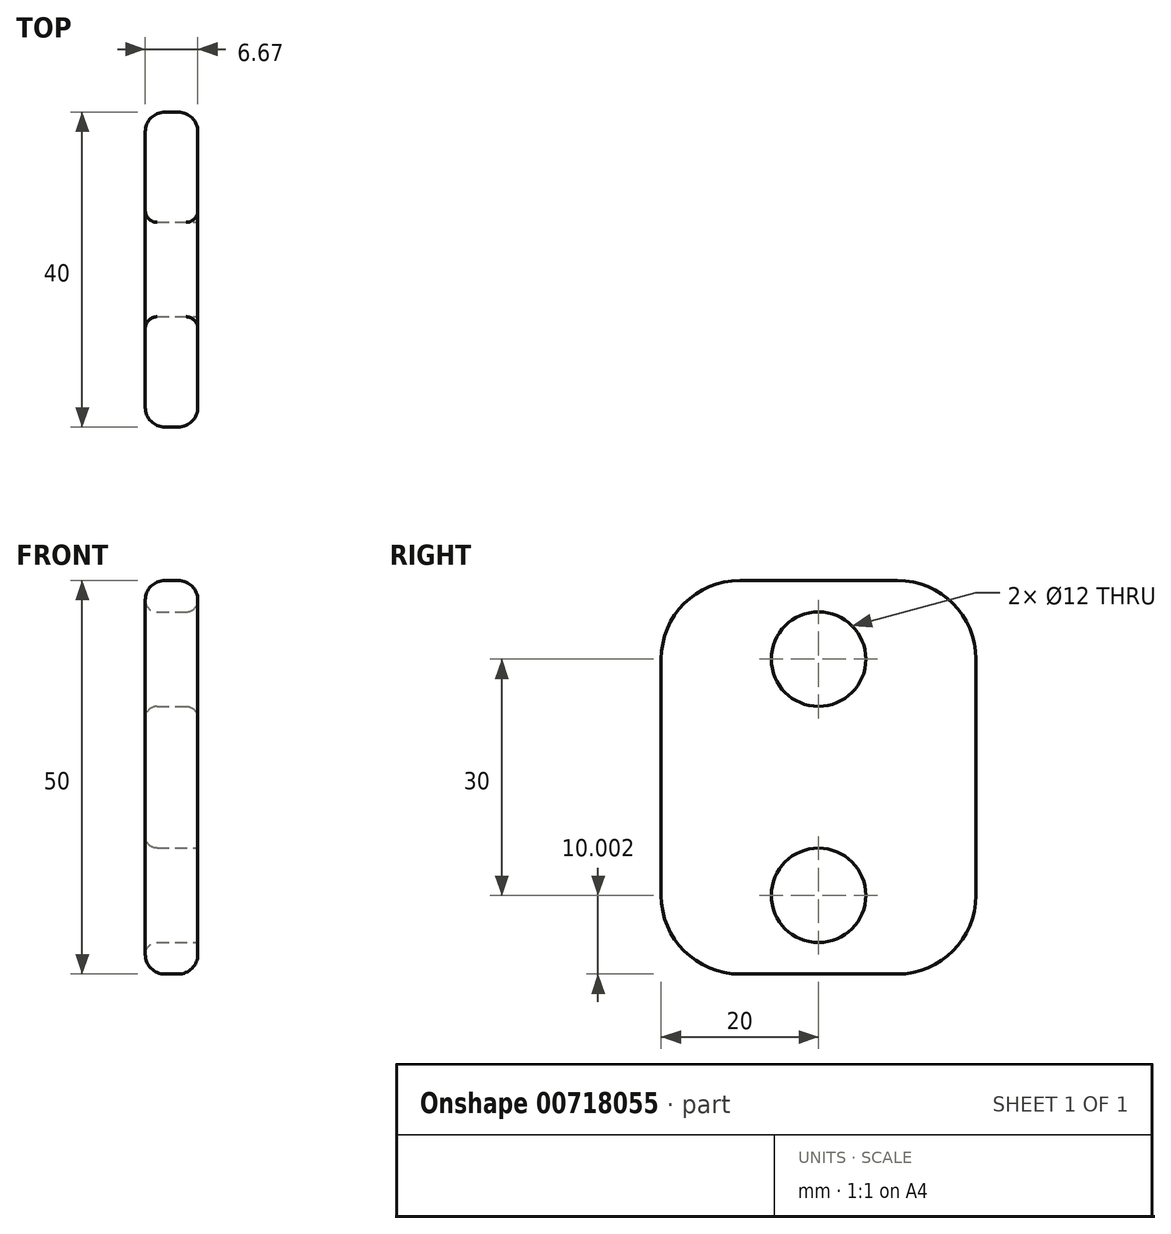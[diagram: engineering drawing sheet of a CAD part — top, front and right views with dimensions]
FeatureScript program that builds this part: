
annotation { "Feature Type Name" : "Feature", "Feature Type Description" : "" }
export const myFeature = defineFeature(function(context is Context, id is Id, definition is map)
    precondition{}
    {
        {
            var Q0;
            Q0=qCreatedBy(makeId("Front.planeOp"),FACE);
            var sketch = newSketch(context, id + "F0", { "sketchPlane" : qUnion([Q0])});
            skLineSegment(sketch, "E0", {"start": v(-3.34, -0.89) * mm, "end": v(-3.34, 19.11) * mm});
            skLineSegment(sketch, "E1", {"start": v(-3.34, 19.11) * mm, "end": v(3.33, 19.11) * mm});
            skLineSegment(sketch, "E2", {"start": v(3.33, 19.11) * mm, "end": v(3.33, -0.89) * mm});
            skLineSegment(sketch, "E3", {"start": v(-3.34, -0.89) * mm, "end": v(-3.34, -30.89) * mm});
            skLineSegment(sketch, "E4", {"start": v(-3.34, -30.89) * mm, "end": v(3.33, -30.89) * mm});
            skLineSegment(sketch, "E5", {"start": v(3.33, -30.89) * mm, "end": v(3.33, 13.67) * mm});
            skLineSegment(sketch, "E6", {"start": v(3.33, -0.89) * mm, "end": v(3.33, 13.67) * mm});
            skSolve(sketch);
        }
        {
            var Q0;
            {var subQ10=sQuery(id+"F0.wireOp",EDGE,"JQoUM4ua-fbHj-mR0V-2uyi-QJGCKq251QAs");Q0=makeQuery(id+"F0.imprint","IMPRINT",FACE,{"disambiguationData":[TD([[makeQuery(id+"F0.imprint","IMPRINT",EDGE,{"derivedFrom":subQ10}),-1.0]])]});}
            var Q1;
            {var subQ0=sQuery(id+"F0.wireOp",EDGE,"E0");Q1=makeQuery(id+"F0.imprint","IMPRINT",FACE,{"disambiguationData":[TD([[makeQuery(id+"F0.imprint","IMPRINT",EDGE,{"derivedFrom":subQ0}),-1.0]])]});}
            var Q2;
            Q2=makeQuery(id+"F0.imprint","IMPRINT",FACE,{"disambiguationData":[TD([[makeQuery(id+"F0.imprint","IMPRINT",EDGE,{"derivedFrom":sQuery(id+"F0.wireOp",EDGE,"YiIlp7im-Q15v-nGEx-m55B-phNHHMeuZ1Th")}),-1.0]])]});
            var Q3;
            {var subQ1=sQuery(id+"F0.wireOp",EDGE,"EbttIiGy-8kt3-poWc-bNZX-1UF2vUk4pGtZ");Q3=makeQuery(id+"F0.imprint","IMPRINT",FACE,{"disambiguationData":[TD([[makeQuery(id+"F0.imprint","IMPRINT",EDGE,{"derivedFrom":subQ1}),1.0]])]});}
            extrude(context, id + "F1", {"entities" : qUnion([Q0, Q1, Q2, Q3]), "depth" : 40 * mm, "offsetDistance" : 25 * mm});
        }
        {
            var Q0;
            Q0=makeQuery(id+"F1.opExtrude","SWEPT_FACE",FACE,{"disambiguationData":[OSD([sQuery(id+"F0.wireOp",EDGE,"E2"),sQuery(id+"F0.wireOp",EDGE,"E5"),sQuery(id+"F0.wireOp",EDGE,"E6")])]});
            var sketch = newSketch(context, id + "F2", { "sketchPlane" : qUnion([Q0])});
            skLineSegment(sketch, "E7", {"start": v(-20, 19.11) * mm, "end": v(-20, -30.89) * mm, "construction": true});
            skLineSegment(sketch, "E8", {"start": v(-20, 19.11) * mm, "end": v(-20, 9.11) * mm, "construction": true});
            skLineSegment(sketch, "E9", {"start": v(-20, 9.11) * mm, "end": v(-20, 0) * mm, "construction": true});
            skLineSegment(sketch, "E10", {"start": v(-20, 0) * mm, "end": v(-20, -10) * mm, "construction": true});
            skLineSegment(sketch, "E11", {"start": v(-20, -10) * mm, "end": v(-20, -20.89) * mm, "construction": true});
            skLineSegment(sketch, "E12", {"start": v(-20, -20.89) * mm, "end": v(-20, -30.89) * mm, "construction": true});
            skCircle(sketch, "E13", {"center": v(-20, 9.11) * mm, "radius": 6 * mm});
            skCircle(sketch, "E14", {"center": v(-20, -20.89) * mm, "radius": 6 * mm});
            skSolve(sketch);
        }
        {
            var Q0;
            Q0=makeQuery(id+"F2.imprint","IMPRINT",FACE,{"disambiguationData":[TD([[makeQuery(id+"F2.imprint","IMPRINT",EDGE,{"derivedFrom":sQuery(id+"F2.wireOp",EDGE,"E13")}),1.0]])]});
            var Q1;
            Q1=makeQuery(id+"F2.imprint","IMPRINT",FACE,{"disambiguationData":[TD([[makeQuery(id+"F2.imprint","IMPRINT",EDGE,{"derivedFrom":sQuery(id+"F2.wireOp",EDGE,"E14")}),1.0]])]});
            extrude(context, id + "F3", {"entities" : qUnion([Q0, Q1]), "operationType" : NewBodyOperationType.REMOVE, "oppositeDirection" : true, "depth" : 25 * mm, "offsetDistance" : 25 * mm});
        }
        {
            var Q0;
            Q0=makeQuery(id+"F1.opExtrude","CAP_EDGE",EDGE,{"disambiguationData":[OSD([sQuery(id+"F0.wireOp",EDGE,"E1")])],"isStart":false});
            var Q1;
            Q1=makeQuery(id+"F1.opExtrude","CAP_EDGE",EDGE,{"disambiguationData":[OSD([sQuery(id+"F0.wireOp",EDGE,"E1")])],"isStart":true});
            var Q2;
            Q2=makeQuery(id+"F1.opExtrude","CAP_EDGE",EDGE,{"disambiguationData":[OSD([sQuery(id+"F0.wireOp",EDGE,"E4")])],"isStart":true});
            var Q3;
            Q3=makeQuery(id+"F1.opExtrude","CAP_EDGE",EDGE,{"disambiguationData":[OSD([sQuery(id+"F0.wireOp",EDGE,"E4")])],"isStart":false});
            fillet(context, id + "F4", {"entities" : qUnion([Q0, Q1, Q2, Q3]), "radius" : 10 * mm, "tangentPropagation" : true, "allowEdgeOverflow" : false});
        }
        {
            var Q0;
            Q0=makeQuery(id+"F1.opExtrude","SWEPT_EDGE",EDGE,{"disambiguationData":[OSD([sQuery(id+"F0.wireOp",EDGE,"E1"),sQuery(id+"F0.wireOp",EDGE,"E2")])]});
            var Q1;
            Q1=makeQuery(id+"F1.opExtrude","SWEPT_EDGE",EDGE,{"disambiguationData":[OSD([sQuery(id+"F0.wireOp",EDGE,"E3"),sQuery(id+"F0.wireOp",EDGE,"E4")])]});
            var Q2;
            Q2=makeQuery(id+"F1.opExtrude","SWEPT_EDGE",EDGE,{"disambiguationData":[OSD([sQuery(id+"F0.wireOp",EDGE,"E0"),sQuery(id+"F0.wireOp",EDGE,"E1")])]});
            var Q3;
            Q3=makeQuery(id+"F4.opFillet","BLEND_EDGE",EDGE,{"blendedFrom":[makeQuery(id+"F1.opExtrude","CAP_EDGE",EDGE,{"disambiguationData":[OSD([sQuery(id+"F0.wireOp",EDGE,"E1")])],"isStart":false}),makeQuery(id+"F1.opExtrude","SWEPT_FACE",FACE,{"disambiguationData":[OSD([sQuery(id+"F0.wireOp",EDGE,"E0"),sQuery(id+"F0.wireOp",EDGE,"E3")])]})],"blendedInto":[makeQuery(id+"F1.opExtrude","SWEPT_FACE",FACE,{"disambiguationData":[OSD([sQuery(id+"F0.wireOp",EDGE,"E0"),sQuery(id+"F0.wireOp",EDGE,"E3")])]})]});
            var Q4;
            Q4=makeQuery(id+"F1.opExtrude","CAP_EDGE",EDGE,{"disambiguationData":[OSD([sQuery(id+"F0.wireOp",EDGE,"E0"),sQuery(id+"F0.wireOp",EDGE,"E3")])],"isStart":false});
            var Q5;
            Q5=makeQuery(id+"F4.opFillet","BLEND_EDGE",EDGE,{"blendedFrom":[makeQuery(id+"F1.opExtrude","CAP_EDGE",EDGE,{"disambiguationData":[OSD([sQuery(id+"F0.wireOp",EDGE,"E4")])],"isStart":false}),makeQuery(id+"F1.opExtrude","SWEPT_FACE",FACE,{"disambiguationData":[OSD([sQuery(id+"F0.wireOp",EDGE,"E0"),sQuery(id+"F0.wireOp",EDGE,"E3")])]})],"blendedInto":[makeQuery(id+"F1.opExtrude","SWEPT_FACE",FACE,{"disambiguationData":[OSD([sQuery(id+"F0.wireOp",EDGE,"E0"),sQuery(id+"F0.wireOp",EDGE,"E3")])]})]});
            var Q6;
            Q6=makeQuery(id+"F4.opFillet","BLEND_EDGE",EDGE,{"blendedFrom":[makeQuery(id+"F1.opExtrude","CAP_EDGE",EDGE,{"disambiguationData":[OSD([sQuery(id+"F0.wireOp",EDGE,"E4")])],"isStart":true}),makeQuery(id+"F1.opExtrude","SWEPT_FACE",FACE,{"disambiguationData":[OSD([sQuery(id+"F0.wireOp",EDGE,"E0"),sQuery(id+"F0.wireOp",EDGE,"E3")])]})],"blendedInto":[makeQuery(id+"F1.opExtrude","SWEPT_FACE",FACE,{"disambiguationData":[OSD([sQuery(id+"F0.wireOp",EDGE,"E0"),sQuery(id+"F0.wireOp",EDGE,"E3")])]})]});
            var Q7;
            Q7=makeQuery(id+"F1.opExtrude","CAP_EDGE",EDGE,{"disambiguationData":[OSD([sQuery(id+"F0.wireOp",EDGE,"E0"),sQuery(id+"F0.wireOp",EDGE,"E3")])],"isStart":true});
            var Q8;
            Q8=makeQuery(id+"F4.opFillet","BLEND_EDGE",EDGE,{"blendedFrom":[makeQuery(id+"F1.opExtrude","CAP_EDGE",EDGE,{"disambiguationData":[OSD([sQuery(id+"F0.wireOp",EDGE,"E1")])],"isStart":true}),makeQuery(id+"F1.opExtrude","SWEPT_FACE",FACE,{"disambiguationData":[OSD([sQuery(id+"F0.wireOp",EDGE,"E0"),sQuery(id+"F0.wireOp",EDGE,"E3")])]})],"blendedInto":[makeQuery(id+"F1.opExtrude","SWEPT_FACE",FACE,{"disambiguationData":[OSD([sQuery(id+"F0.wireOp",EDGE,"E0"),sQuery(id+"F0.wireOp",EDGE,"E3")])]})]});
            fillet(context, id + "F5", {"entities" : qUnion([Q0, Q1, Q2, Q3, Q4, Q5, Q6, Q7, Q8]), "radius" : 2.5 * mm, "tangentPropagation" : true, "allowEdgeOverflow" : false});
        }
        {
            var Q0;
            Q0=makeQuery(id+"F3.boolean.opBoolean","COPY",EDGE,{"derivedFrom":makeQuery(id+"F3.opExtrude","CAP_EDGE",EDGE,{"disambiguationData":[OSD([sQuery(id+"F2.wireOp",EDGE,"E13")])],"isStart":true})});
            var Q1;
            Q1=makeQuery(id+"F3.boolean.opBoolean","COPY",FACE,{"derivedFrom":makeQuery(id+"F3.opExtrude","SWEPT_FACE",FACE,{"disambiguationData":[OSD([sQuery(id+"F2.wireOp",EDGE,"E13")])]})});
            var Q2;
            Q2=makeQuery(id+"F3.boolean.opBoolean","COPY",EDGE,{"derivedFrom":makeQuery(id+"F3.opExtrude","CAP_EDGE",EDGE,{"disambiguationData":[OSD([sQuery(id+"F2.wireOp",EDGE,"E14")])],"isStart":true})});
            var Q3;
            Q3=makeQuery(id+"F3.boolean.opBoolean","INTERSECT",EDGE,{"derivedFrom":[makeQuery(id+"F1.opExtrude","SWEPT_FACE",FACE,{"disambiguationData":[OSD([sQuery(id+"F0.wireOp",EDGE,"E0"),sQuery(id+"F0.wireOp",EDGE,"E3")])]}),makeQuery(id+"F3.opExtrude","SWEPT_FACE",FACE,{"disambiguationData":[OSD([sQuery(id+"F2.wireOp",EDGE,"E14")])]})]});
            fillet(context, id + "F6", {"entities" : qUnion([Q0, Q1, Q2, Q3]), "radius" : 1.5 * mm, "tangentPropagation" : true, "allowEdgeOverflow" : false});
        }
    });
